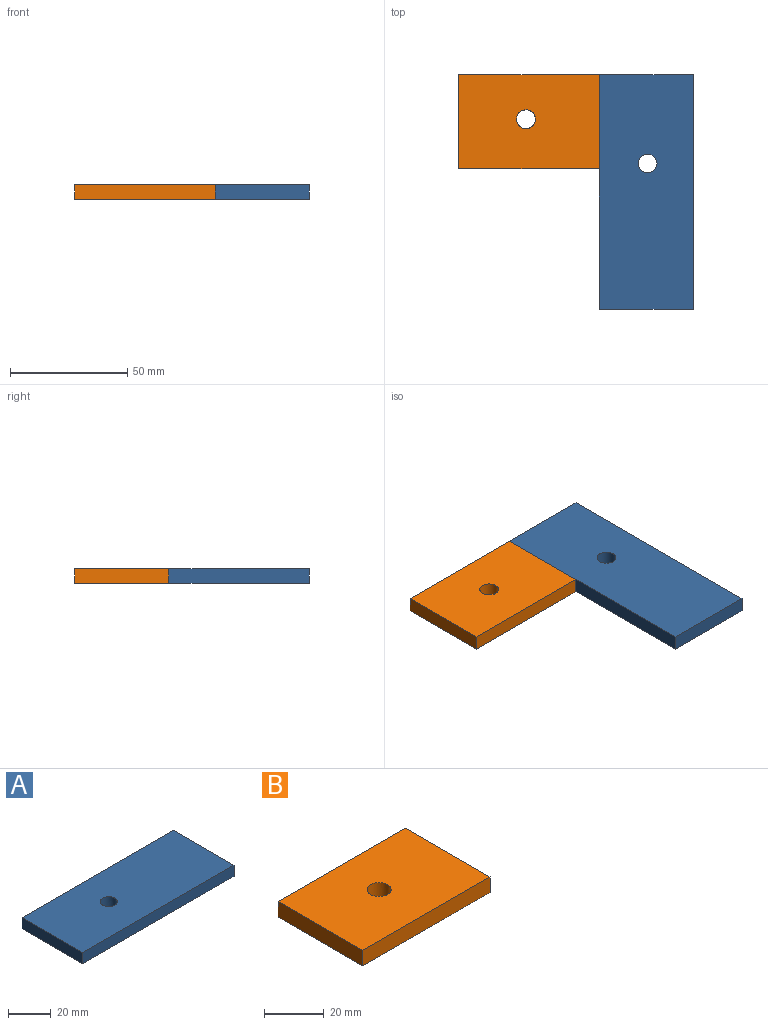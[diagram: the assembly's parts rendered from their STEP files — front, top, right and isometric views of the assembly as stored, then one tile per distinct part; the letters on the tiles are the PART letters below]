
ASSEMBLY  parts=2 mates=1
PART A: 7 faces, bbox 100x40x6.4 mm
  f0: plane 100x6.35mm, normal (0,1,0), area 635mm2, adj f1,f3,f4,f5
  f1: plane 40x6.35mm, normal (-1,0,0), area 254mm2, adj f0,f2,f4,f5
  f2: plane 100x6.35mm, normal (0,-1,0), area 635mm2, adj f1,f3,f4,f5
  f3: plane 40x6.35mm, normal (1,0,0), area 254mm2, adj f0,f2,f4,f5
  f4: plane 100x40mm, normal (0,0,1), area 3949.7mm2, adj f0,f1,f2,f3,f6
  f5: plane 100x40mm, normal (0,0,-1), area 3949.7mm2, adj f0,f1,f2,f3,f6
  f6: cylinder r=4mm len=8mm, axis (0,0,-1), area 159.6mm2, adj f4,f5
PART B: 7 faces, bbox 60x40x6.4 mm
  f0: plane 60x6.35mm, normal (0,1,0), area 381mm2, adj f1,f3,f4,f5
  f1: plane 40x6.35mm, normal (-1,0,0), area 254mm2, adj f0,f2,f4,f5
  f2: plane 60x6.35mm, normal (0,-1,0), area 381mm2, adj f1,f3,f4,f5
  f3: plane 40x6.35mm, normal (1,0,0), area 254mm2, adj f0,f2,f4,f5
  f4: plane 60x40mm, normal (0,0,1), area 2349.7mm2, adj f0,f1,f2,f3,f6
  f5: plane 60x40mm, normal (0,0,-1), area 2349.7mm2, adj f0,f1,f2,f3,f6
  f6: cylinder r=4mm len=8mm, axis (0,0,-1), area 159.6mm2, adj f4,f5
PLACE A rot(axis=(0,0,-1),90deg) t=(-36.82,17.92,20.74)mm
PLACE B t=(-36.68,57.29,20.74)mm
MATE fastened A.f2 <-> B.f3  axis (-1,0,0) through (-36.7,97.26,20.74)mm
